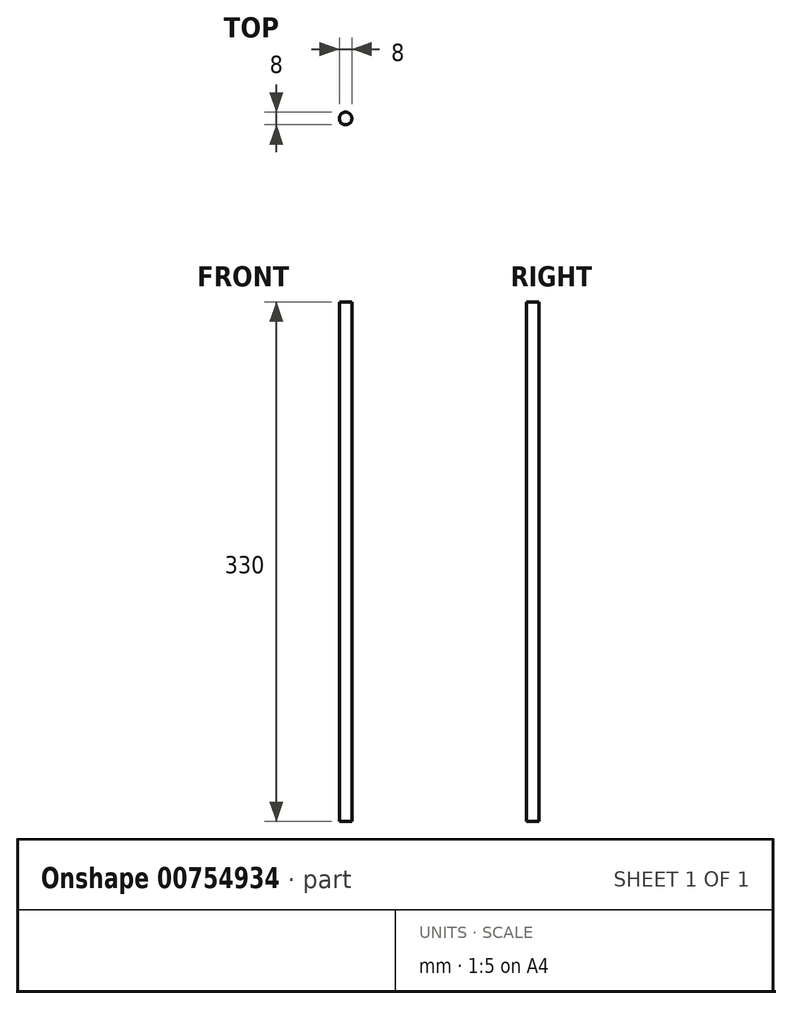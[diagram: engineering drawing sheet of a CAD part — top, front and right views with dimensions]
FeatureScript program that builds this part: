
annotation { "Feature Type Name" : "Feature", "Feature Type Description" : "" }
export const myFeature = defineFeature(function(context is Context, id is Id, definition is map)
    precondition{}
    {
        {
            var Q0;
            Q0=qCreatedBy(makeId("Top.planeOp"),FACE);
            var sketch = newSketch(context, id + "F0", { "sketchPlane" : qUnion([Q0])});
            skCircle(sketch, "E0", {"center": v(0, 0) * mm, "radius": 4 * mm});
            skSolve(sketch);
        }
        {
            var Q0;
            Q0=makeQuery(id+"F0.imprint","IMPRINT",FACE,{"disambiguationData":[TD([[makeQuery(id+"F0.imprint","IMPRINT",EDGE,{"derivedFrom":sQuery(id+"F0.wireOp",EDGE,"E0")}),1.0]])]});
            extrude(context, id + "F1", {"entities" : qUnion([Q0]), "depth" : 330 * mm, "offsetDistance" : 25 * mm});
        }
    });
